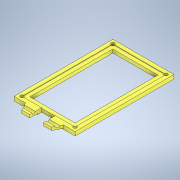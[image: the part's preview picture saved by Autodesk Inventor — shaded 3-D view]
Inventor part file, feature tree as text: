
AUTODESK INVENTOR PART (.ipt)
format: ipt  version: 2022 (Build 260153000, 153)  size: 183,296 bytes
history: native  units: mm
features: extrude x5, sketch x5
ambient origin geometry x8: Origin, YZ Plane, XZ Plane, XY Plane, X Axis, Y Axis, Z Axis, Center Point
bodies: 实体1 (feature_tree)
feature tree (10):
  extrude  "拉伸1"  Depth=61.8mm
  extrude  "拉伸2"  Depth=8.0mm
  extrude  "拉伸3"  Depth=4.0mm
  extrude  "拉伸4"  Depth=92.0mm
  extrude  "拉伸5"  Depth=8.0mm
  sketch  "草图1"  dims[d0=100.0mm d1=61.8mm]
  sketch  "草图2"  dims[d2=8.0mm d3=8.0mm]
  sketch  "草图3"  dims[d4=3.5mm d5=4.0mm]
  sketch  "草图4"  dims[d6=4.0mm d7=20.0mm d9=92.0mm d10=20.0mm d12=53.8mm]
  sketch  "草图5"  dims[d15=4.0mm d16=0.0mm d17=8.0mm d18=30.0mm d19=3.0mm d20=0.0mm d21=3.2mm d22=40.0mm d23=40.0mm d24=0.0mm d25=0.0mm d26=12.0mm d27=14.0mm d28=40.0mm d29=0.0mm d30=0.5mm d31=0.0mm]
